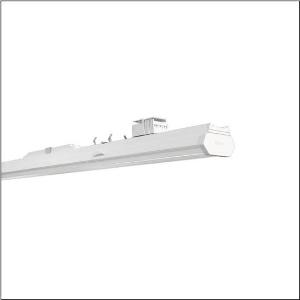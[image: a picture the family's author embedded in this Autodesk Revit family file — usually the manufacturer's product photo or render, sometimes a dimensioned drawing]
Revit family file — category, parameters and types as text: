
# Revit family: licross_r__21_protected_mo_52ts12dnd7xf_9118
name_source: partatom
category: Lighting Fixtures
units: mm (PartAtom-declared; Revit-internal decimal feet)

## family parameters
Cut with Voids When Loaded = No
Host = Face
Light Source = No
Part Type = Normal
Room Calculation Point = No
Round Connector Dimension = Use Diameter
Shared = No

## types (1)
- --- (1 x LED, 7240 lm, 60.9 W, 4000K)
    Apparent Load = 61 VA
    CIE Flux Codes = 54 82 95 97 100
    Color Rendering = 90
    Color Temperature = 4000K
    Default Elevation = 1800 mm
    Description = Licross® 21 Protected MO, luminaire insert, of sheet steel, galvanised, coil coated, white, length: 1.500mm, width: 90mm, height: 101mm, LED rated luminous flux: 7.240lm, light colour: 940, control gear: DALI 2, control gear: ECG DALI, with plug, 5-pole, with phase selection, mains connection: 220..240V, AC, 50/60Hz, rated input power: 61W, halogen-free wiring, primary optical cover: cover, of PMMA, light emission: direct distribution, primary light characteristic: symmetric, protection rating (complete): IP50, insulation class (complete): insulation class I (protective earthing), certification: CE, ENEC, VDE, UKCA, protection symbol: D if used in an environment with non-conductive dust loads with corresponding accessories, impact resistance: IK06, permissible ambient temperature for indoor applications: -25..+40°C, corresponds to IFS (International Featured Standards) requirements for safety and quality in the food industry, reducing of maximum allowable ambient temperature of 5°C with ceiling mounting, LABS conformity tested according to VDMA 24364:2018-05, packaging unit: 1 piece
    Height = 92 mm
    Lamp = 1 x LED
    Lamp Light Flux = 7240 lm
    Lamp Power = 60.9 W
    Lamp count = 1
    Length = 1500 mm
    Luminous efficacy = 119 lm/W
    Manufacturer = Siteco
    ModVariant = No
    Model = 52TS12DND7XF
    Mounting Place = Ceiling
    Mounting Type = Pendant
    Number of Poles = 1
    OnlyDefault = Yes
    Power Factor = 1
    Product Name = Licross® 21 Protected MO
    Product group = luminaire insert
    ProductGroupID = 901
    Protection Class = Protection class I
    Protection Degree = IP 50
    RLX_Detail_Level = 1
    RLX_Emergency_Light_Flux = 0 lm
    RLX_Emergency_Type = 0
    RLX_Emergency_Type_DB = No
    RlxData = <blob elided: 24253 chars, md5=bbbc01ba>
    Socket = socket
    Standby Power = 0 W
    System Light Flux = 7240 lm
    System Power = 61 W
    Type Comments = factory setting: luminous flux: 100 % | dim-lin: 254 | 405 mA
    Type Image = l_1256145.jpg
    URL = http://relux.com
    VarID = @adj_136611
    Voltage = 0 V
    Weight = 0.00 kg
    Width = 88 mm

## geometry (parser evidence)
native form markers: Blend x4, Sweep x12
no freeform markers — native parametric forms only
